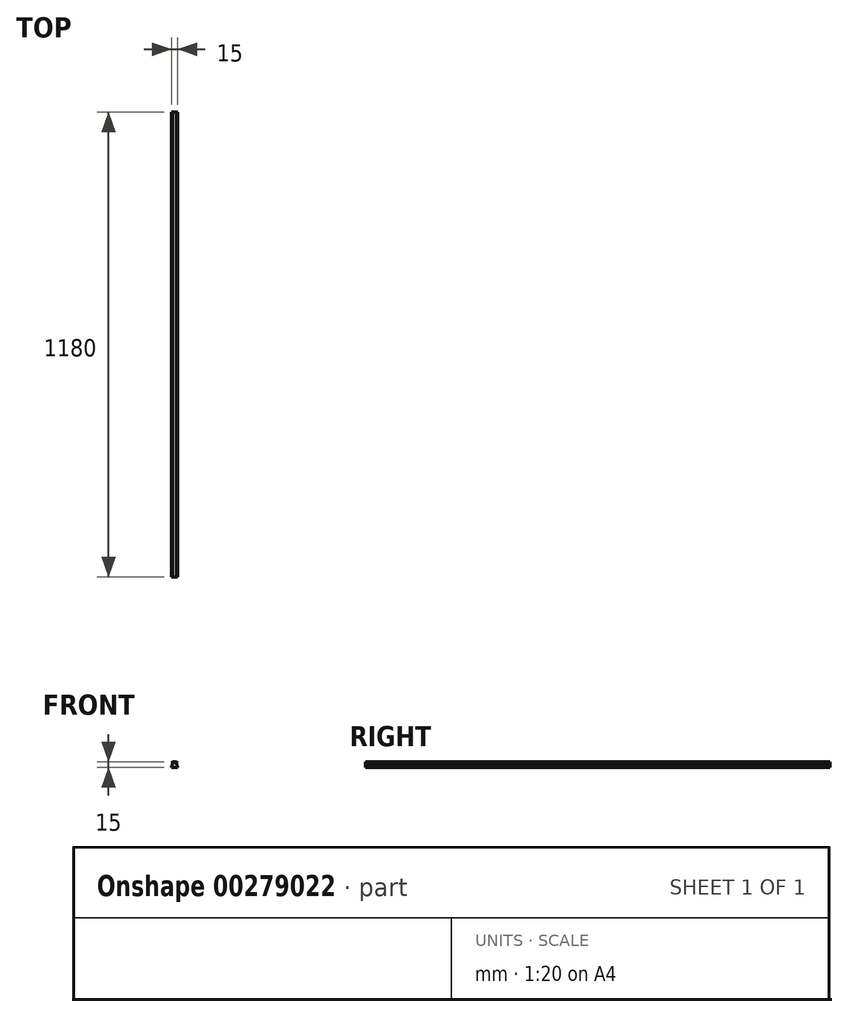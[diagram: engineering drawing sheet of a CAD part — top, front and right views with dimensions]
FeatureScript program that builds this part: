
annotation { "Feature Type Name" : "Feature", "Feature Type Description" : "" }
export const myFeature = defineFeature(function(context is Context, id is Id, definition is map)
    precondition{}
    {
        {
            var Q0;
            Q0=qCreatedBy(makeId("Front.planeOp"),FACE);
            var sketch = newSketch(context, id + "F0", { "sketchPlane" : qUnion([Q0])});
            skLineSegment(sketch, "E0", {"start": v(-7.5, 0) * mm, "end": v(-7.5, 4.3) * mm});
            skLineSegment(sketch, "E1", {"start": v(-7.5, 4.3) * mm, "end": v(-3.7, 4.3) * mm, "construction": true});
            skLineSegment(sketch, "E2", {"start": v(-7.5, 4.3) * mm, "end": v(-5.38, 6.42) * mm});
            skLineSegment(sketch, "E3", {"start": v(-5.38, 6.42) * mm, "end": v(-5.38, 9.42) * mm});
            skLineSegment(sketch, "E4", {"start": v(-9.32, 7.92) * mm, "end": v(-5.38, 7.92) * mm, "construction": true});
            skLineSegment(sketch, "E5", {"start": v(-5.38, 9.42) * mm, "end": v(-7.5, 11.54) * mm});
            skLineSegment(sketch, "E6", {"start": v(-7.5, 11.54) * mm, "end": v(-7.5, 12.54) * mm});
            skLineSegment(sketch, "E7", {"start": v(-7.5, 12.54) * mm, "end": v(-2.34, 12.54) * mm, "construction": true});
            skLineSegment(sketch, "E8", {"start": v(-7.5, 12.54) * mm, "end": v(-5.04, 15) * mm});
            skLineSegment(sketch, "E9", {"start": v(0, -1.94) * mm, "end": v(0, 16.94) * mm, "construction": true});
            skLineSegment(sketch, "E10", {"start": v(7.5, 0) * mm, "end": v(7.5, 4.3) * mm});
            skLineSegment(sketch, "E11", {"start": v(7.5, 4.3) * mm, "end": v(3.77, 4.3) * mm, "construction": true});
            skLineSegment(sketch, "E12", {"start": v(7.5, 4.3) * mm, "end": v(5.38, 6.42) * mm});
            skLineSegment(sketch, "E13", {"start": v(5.38, 6.42) * mm, "end": v(5.38, 9.42) * mm});
            skLineSegment(sketch, "E14", {"start": v(5.38, 9.42) * mm, "end": v(7.5, 11.54) * mm});
            skLineSegment(sketch, "E15", {"start": v(7.5, 11.54) * mm, "end": v(7.5, 12.54) * mm});
            skLineSegment(sketch, "E16", {"start": v(7.5, 12.54) * mm, "end": v(5.04, 15) * mm});
            skLineSegment(sketch, "E17", {"start": v(7.5, 12.54) * mm, "end": v(3.67, 12.54) * mm, "construction": true});
            skLineSegment(sketch, "E18", {"start": v(7.5, 11.54) * mm, "end": v(3.7, 11.54) * mm, "construction": true});
            skLineSegment(sketch, "E19", {"start": v(-7.5, 11.54) * mm, "end": v(-3.2, 11.54) * mm, "construction": true});
            skLineSegment(sketch, "E20", {"start": v(-5.04, 15) * mm, "end": v(5.04, 15) * mm});
            skLineSegment(sketch, "E21", {"start": v(-7.5, 0) * mm, "end": v(7.5, 0) * mm});
            skSolve(sketch);
        }
        {
            var Q0;
            Q0=makeQuery(id+"F0.imprint","IMPRINT",FACE,{"disambiguationData":[TD([[makeQuery(id+"F0.imprint","IMPRINT",EDGE,{"derivedFrom":sQuery(id+"F0.wireOp",EDGE,"E0")}),-1.0]])]});
            extrude(context, id + "F1", {"entities" : qUnion([Q0]), "endBound" : BoundingType.SYMMETRIC, "depth" : 1180 * mm});
        }
    });
